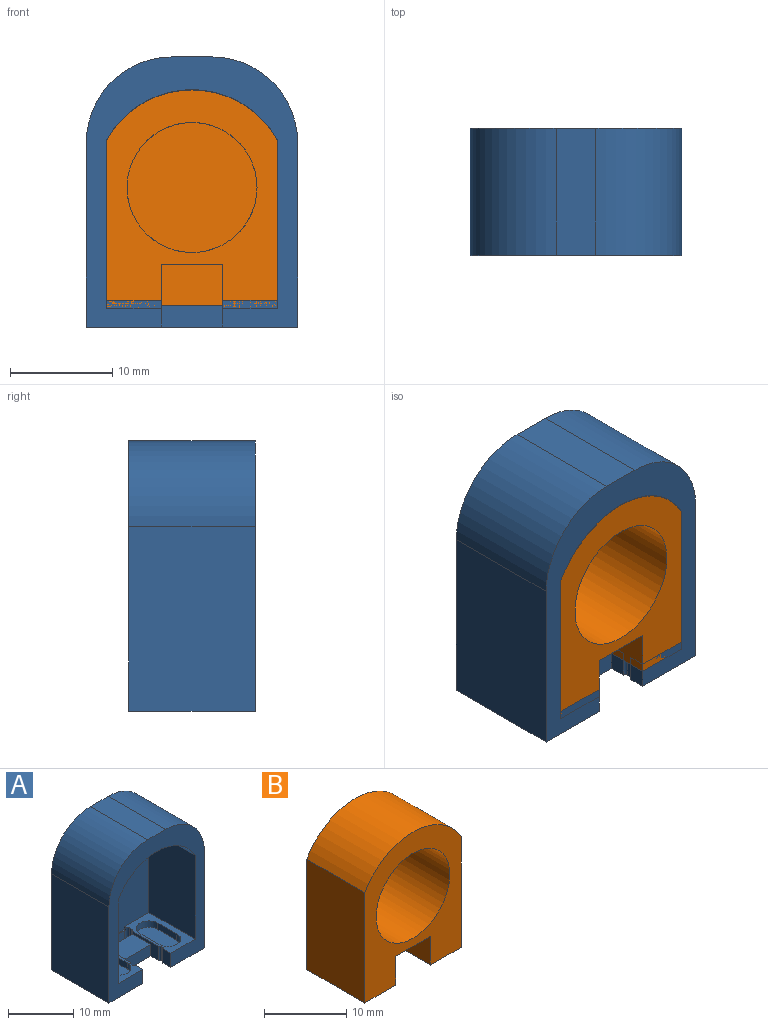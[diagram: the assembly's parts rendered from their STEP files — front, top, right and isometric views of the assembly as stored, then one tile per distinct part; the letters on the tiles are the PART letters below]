
ASSEMBLY  parts=2 mates=1
PART A: 47 faces, bbox 20.7x12.4x26.4 mm
  f0: plane 5.64x2.63mm, normal (-1,0,0), area 6.3mm2, adj f6,f12,f17,f23,f33,f46
  f1: plane 5.64x2.63mm, normal (1,0,0), area 6.3mm2, adj f6,f10,f19,f23,f32,f46
  f2: plane 26.38x20.65mm, normal (0,-1,0), area 180.1mm2, adj f4,f5,f25,f26,f27,f28,f29,f30
  f3: plane 26.38x20.65mm, normal (0,1,0), area 514.6mm2, adj f25,f26,f30,f44,f45,f46
  f4: plane 2.63x1.65mm, normal (-1,0,0), area 4.3mm2, adj f2,f11,f33,f46
  f5: plane 2.63x1.65mm, normal (1,0,0), area 4.3mm2, adj f2,f9,f32,f46
  f6: plane 6x2.14mm, normal (0,-1,0), area 12.8mm2, adj f0,f1,f23,f46
  f7: plane 2.63x0.4mm, normal (1,0,0), area 1.1mm2, adj f9,f10,f32,f46
  f8: plane 2.63x0.4mm, normal (-1,0,0), area 1.1mm2, adj f11,f12,f33,f46
  f9: cylinder r=0.3mm len=2.63mm, axis (0,0,-1), area 1.2mm2, adj f5,f7,f32,f46
  f10: cylinder r=0.3mm len=2.63mm, axis (0,0,1), area 1.2mm2, adj f1,f7,f32,f46
  f11: cylinder r=0.3mm len=2.63mm, axis (0,0,1), area 1.2mm2, adj f4,f8,f33,f46
  f12: cylinder r=0.3mm len=2.63mm, axis (0,0,-1), area 1.2mm2, adj f0,f8,f33,f46
  f13: plane 2.63x0.5mm, normal (-1,0,0), area 1.3mm2, adj f17,f18,f33,f46
  f14: plane 5.6x2.14mm, normal (0,1,0), area 12mm2, adj f17,f19,f23,f46
  f15: plane 5.6x2.14mm, normal (0,-1,0), area 12mm2, adj f18,f20,f24,f46
  f16: plane 2.63x0.5mm, normal (1,0,0), area 1.3mm2, adj f19,f20,f32,f46
  f17: cylinder r=0.5mm len=2.63mm, axis (0,0,1), area 2mm2, adj f0,f13,f14,f23,f33,f46
  f18: cylinder r=0.5mm len=2.63mm, axis (0,0,1), area 2mm2, adj f13,f15,f21,f24,f33,f46
  f19: cylinder r=0.5mm len=2.63mm, axis (0,0,-1), area 2mm2, adj f1,f14,f16,f23,f32,f46
  f20: cylinder r=0.5mm len=2.63mm, axis (0,0,-1), area 2mm2, adj f15,f16,f22,f24,f32,f46
  f21: plane 0.48x0.29mm, normal (-1,0,0), area 0.1mm2, adj f18,f24,f31,f33
  f22: plane 0.48x0.29mm, normal (1,0,0), area 0.1mm2, adj f20,f24,f31,f32
  f23: plane 6x3.99mm, normal (0,0,1), area 23.7mm2, adj f0,f1,f6,f14,f17,f19
  f24: plane 6x0.29mm, normal (0,0,1), area 1.5mm2, adj f15,f18,f20,f21,f22,f31
  f25: plane 12.4x3.89mm, normal (0,0,1), area 48.2mm2, adj f2,f3,f44,f45
  f26: plane 18x12.4mm, normal (-1,0,0), area 223.2mm2, adj f2,f3,f45,f46
  f27: plane 15.67x10mm, normal (1,0,0), area 156.7mm2, adj f2,f28,f31,f32
  f28: cylinder r=9.53mm len=16.65mm, axis (0,1,0), area 202.6mm2, adj f2,f27,f29,f31
  f29: plane 15.67x10mm, normal (-1,0,0), area 156.7mm2, adj f2,f28,f31,f33
  f30: plane 18x12.4mm, normal (1,0,0), area 223.2mm2, adj f2,f3,f44,f46
  f31: plane 21.05x16.65mm, normal (0,-1,0), area 321.7mm2, adj f21,f22,f24,f27,f28,f29,f32,f33
  f32: plane 10x5.33mm, normal (0,0,1), area 24.7mm2, adj f1,f2,f5,f7,f9,f10,f16,f19
  f33: plane 10x5.33mm, normal (0,0,1), area 24.7mm2, adj f0,f2,f4,f8,f11,f12,f13,f17
  f34: plane 4.1x1.2mm, normal (1,0,0), area 4.9mm2, adj f33,f36,f42,f43
  f35: plane 4.1x1.2mm, normal (-1,0,0), area 4.9mm2, adj f33,f36,f42,f43
  f36: plane 8x3.9mm, normal (0,0,1), area 27.9mm2, adj f34,f35,f42,f43
  f37: plane 4.1x1.2mm, normal (1,0,0), area 4.9mm2, adj f32,f39,f40,f41
  f38: plane 4.1x1.2mm, normal (-1,0,0), area 4.9mm2, adj f32,f39,f40,f41
  f39: plane 8x3.9mm, normal (0,0,1), area 27.9mm2, adj f37,f38,f40,f41
  f40: cylinder r=1.95mm len=3.9mm, axis (0,0,1), area 7.4mm2, adj f32,f37,f38,f39
  f41: cylinder r=1.95mm len=3.9mm, axis (0,0,1), area 7.4mm2, adj f32,f37,f38,f39
  f42: cylinder r=1.95mm len=3.9mm, axis (0,0,1), area 7.4mm2, adj f33,f34,f35,f36
  f43: cylinder r=1.95mm len=3.9mm, axis (0,0,1), area 7.4mm2, adj f33,f34,f35,f36
  f44: cylinder r=8.38mm len=12.4mm, axis (0,-1,0), area 163.3mm2, adj f2,f3,f25,f30
  f45: cylinder r=8.38mm len=12.4mm, axis (0,1,0), area 163.3mm2, adj f2,f3,f25,f26
  f46: plane 20.65x12.4mm, normal (0,0,-1), area 220.1mm2, adj f0,f1,f2,f3,f4,f5,f6,f7
PART B: 22 faces, bbox 16.7x10x21.4 mm
  f0: plane 16.48x10mm, normal (1,0,0), area 164.8mm2, adj f2,f3,f7,f11
  f1: plane 16.48x10mm, normal (-1,0,0), area 164.8mm2, adj f2,f3,f7,f11
  f2: plane 21.38x16.65mm, normal (0,1,0), area 332.3mm2, adj f0,f1,f7,f11
  f3: plane 21.38x16.65mm, normal (0,-1,0), area 179.8mm2, adj f0,f1,f5,f6,f7,f8,f10,f11
  f4: plane 6x4.3mm, normal (0,-1,0), area 25.8mm2, adj f5,f6,f10,f11
  f5: plane 7x4.3mm, normal (-1,0,0), area 30.1mm2, adj f3,f4,f10,f11
  f6: plane 7x4.3mm, normal (1,0,0), area 30.1mm2, adj f3,f4,f10,f11
  f7: cylinder r=9.53mm len=16.65mm, axis (0,1,0), area 202.6mm2, adj f0,f1,f2,f3
  f8: cylinder r=6.35mm len=12.7mm, axis (0,1,0), area 359.1mm2, adj f3,f9
  f9: plane 12.7x12.7mm, normal (0,-1,0), area 126.7mm2, adj f8
  f10: plane 7x6mm, normal (0,0,-1), area 42mm2, adj f3,f4,f5,f6
  f11: plane 16.65x10mm, normal (0,0,-1), area 68.6mm2, adj f0,f1,f2,f3,f4,f5,f6,f12
  f12: plane 4.1x1.2mm, normal (1,0,0), area 4.9mm2, adj f11,f14,f18,f19
  f13: plane 4.1x1.2mm, normal (-1,0,0), area 4.9mm2, adj f11,f14,f18,f19
  f14: plane 8x3.9mm, normal (0,0,-1), area 27.9mm2, adj f12,f13,f18,f19
  f15: plane 4.1x1.2mm, normal (1,0,0), area 4.9mm2, adj f11,f17,f20,f21
  f16: plane 4.1x1.2mm, normal (-1,0,0), area 4.9mm2, adj f11,f17,f20,f21
  f17: plane 8x3.9mm, normal (0,0,-1), area 27.9mm2, adj f15,f16,f20,f21
  f18: cylinder r=1.95mm len=3.9mm, axis (0,0,1), area 7.4mm2, adj f11,f12,f13,f14
  f19: cylinder r=1.95mm len=3.9mm, axis (0,0,1), area 7.4mm2, adj f11,f12,f13,f14
  f20: cylinder r=1.95mm len=3.9mm, axis (0,0,-1), area 7.4mm2, adj f11,f15,f16,f17
  f21: cylinder r=1.95mm len=3.9mm, axis (0,0,-1), area 7.4mm2, adj f11,f15,f16,f17
PLACE A t=(-1.87,5,1.26)mm
PLACE B t=(-1.87,5,1.22)mm
MATE planar A.f31 <-> B.f2  axis (0,-1,0) through (-1.87,5,-0.25)mm
